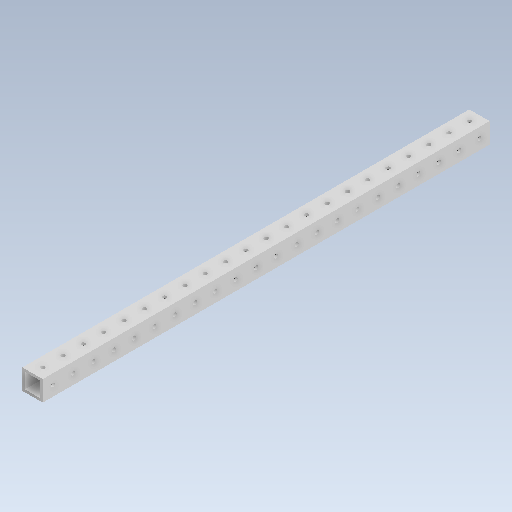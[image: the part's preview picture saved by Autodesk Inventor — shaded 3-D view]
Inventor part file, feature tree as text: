
AUTODESK INVENTOR PART (.ipt)
format: ipt  version: 2020 (Build 240168000, 168)  size: 255,488 bytes
history: native  units: in
note: dims shown in document units (in); Inventor stores cm internally (conversion verified against a paired STEP export)
features: extrude x3, sketch x3
ambient origin geometry x8: Origin, YZ Plane, XZ Plane, XY Plane, X Axis, Y Axis, Z Axis, Center Point
bodies: Solid1 (feature_tree)
feature tree (6):
  extrude  "Extrusion1"  Depth=1.0in
  extrude  "Extrusion2"  Depth=22.0in TaperAngle=0.0deg
  extrude  "Extrusion3"  Depth=1.0in
  sketch  "Sketch1"  dims[d0=1.0in d1=1.0in]
  sketch  "Sketch2"  dims[d2=0.125in d3=22.0in d4=0.0in]
  sketch  "Sketch3"  dims[d5=0.5in d6=0.5in d7=0.2in d8=8.6614in d10=1.0in d11=0.3937in d13=1.0in d15=0.0in d16=0.0in d17=0.5in d18=0.5in d19=0.2in d20=8.6614in d22=1.0in d23=0.3937in d25=1.0in d27=0.0in d28=0.0in]
